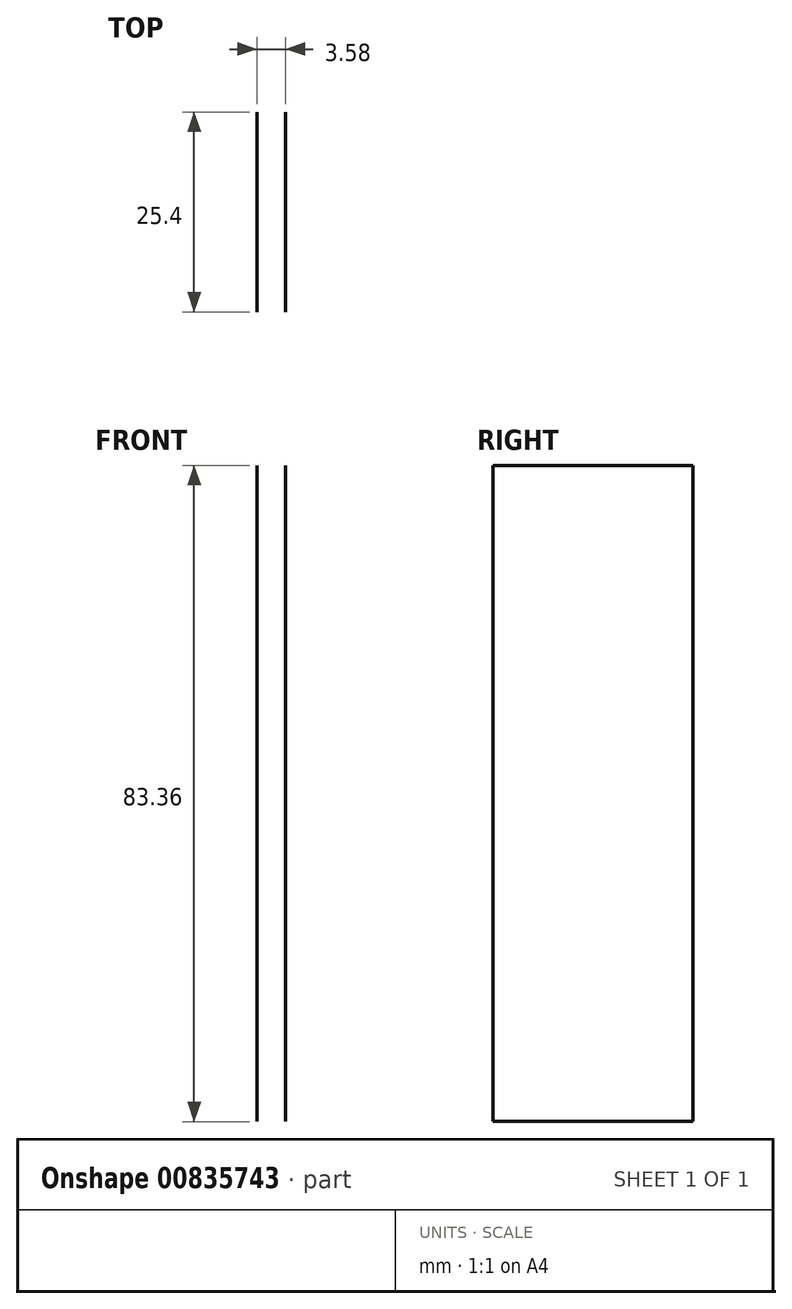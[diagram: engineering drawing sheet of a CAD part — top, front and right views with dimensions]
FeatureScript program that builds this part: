
annotation { "Feature Type Name" : "Feature", "Feature Type Description" : "" }
export const myFeature = defineFeature(function(context is Context, id is Id, definition is map)
    precondition{}
    {
        {
            var Q0;
            Q0=qCreatedBy(makeId("Front.planeOp"),FACE);
            var sketch = newSketch(context, id + "F0", { "sketchPlane" : qUnion([Q0])});
            skLineSegment(sketch, "E0.bottom", {"start": v(0, -54.96) * mm, "end": v(-3.58, -54.96) * mm});
            skLineSegment(sketch, "E0.top", {"start": v(0, 28.4) * mm, "end": v(-3.58, 28.4) * mm});
            skLineSegment(sketch, "E0.left", {"start": v(0, -54.96) * mm, "end": v(0, 28.4) * mm});
            skLineSegment(sketch, "E0.right", {"start": v(-3.58, -54.96) * mm, "end": v(-3.58, 28.4) * mm});
            skLineSegment(sketch, "E1.bottom", {"start": v(-19.28, 46.64) * mm, "end": v(16.05, 46.64) * mm});
            skLineSegment(sketch, "E1.top", {"start": v(-19.28, 28.4) * mm, "end": v(16.05, 28.4) * mm});
            skLineSegment(sketch, "E1.left", {"start": v(-19.28, 46.64) * mm, "end": v(-19.28, 28.4) * mm});
            skLineSegment(sketch, "E1.right", {"start": v(16.05, 46.64) * mm, "end": v(16.05, 28.4) * mm});
            skSolve(sketch);
        }
        {
            var Q0;
            Q0=sQuery(id+"F0.wireOp",EDGE,"E0.left");
            var Q1;
            Q1=sQuery(id+"F0.wireOp",EDGE,"E0.right");
            extrude(context, id + "F1", {"bodyType" : ToolBodyType.SURFACE, "surfaceEntities" : qUnion([Q0, Q1]), "depth" : 25.4 * mm, "offsetDistance" : 25.4 * mm});
        }
    });
